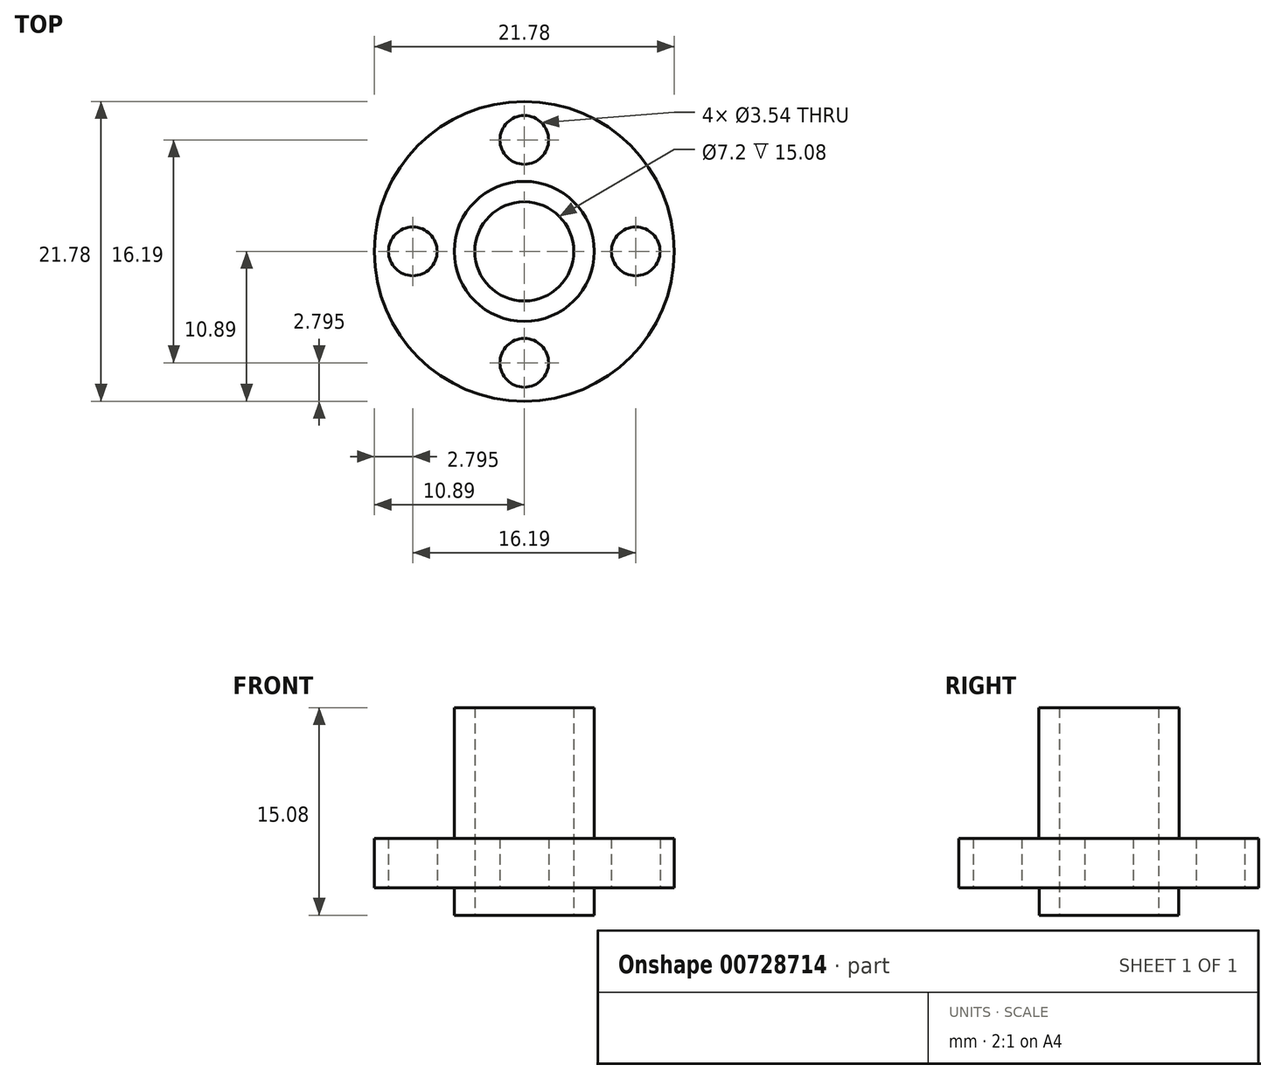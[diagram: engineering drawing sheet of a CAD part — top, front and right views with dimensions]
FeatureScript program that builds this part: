
annotation { "Feature Type Name" : "Feature", "Feature Type Description" : "" }
export const myFeature = defineFeature(function(context is Context, id is Id, definition is map)
    precondition{}
    {
        {
            var Q0;
            Q0=qCreatedBy(makeId("Top.planeOp"),FACE);
            var sketch = newSketch(context, id + "F0", { "sketchPlane" : qUnion([Q0])});
            skCircle(sketch, "E0", {"center": v(0, 0) * mm, "radius": 10.9 * mm});
            skCircle(sketch, "E1", {"center": v(0, 0) * mm, "radius": 8.1 * mm, "construction": true});
            skCircle(sketch, "E2", {"center": v(0, 8.1) * mm, "radius": 1.77 * mm});
            skCircle(sketch, "E3.1.0", {"center": v(8.1, 0) * mm, "radius": 1.77 * mm});
            skCircle(sketch, "E3.2.0", {"center": v(0, -8.1) * mm, "radius": 1.77 * mm});
            skCircle(sketch, "E3.3.0", {"center": v(-8.1, 0) * mm, "radius": 1.77 * mm});
            skLineSegment(sketch, "E3.anchor1", {"start": v(0, 0) * mm, "end": v(0, 8.1) * mm, "construction": true});
            skLineSegment(sketch, "E3.anchor2", {"start": v(0, 0) * mm, "end": v(-8.1, 0) * mm, "construction": true});
            skCircle(sketch, "E4", {"center": v(0, 0) * mm, "radius": 3.6 * mm});
            skSolve(sketch);
        }
        {
            var Q0;
            Q0=makeQuery(id+"F0.imprint","IMPRINT",FACE,{"disambiguationData":[TD([[makeQuery(id+"F0.imprint","IMPRINT",EDGE,{"derivedFrom":sQuery(id+"F0.wireOp",EDGE,"E0")}),1.0]])]});
            extrude(context, id + "F1", {"entities" : qUnion([Q0]), "depth" : 3.58 * mm, "offsetDistance" : 25 * mm});
        }
        {
            var Q0;
            Q0=makeQuery(id+"F1.opExtrude","CAP_FACE",FACE,{"disambiguationData":[OSD([sQuery(id+"F0.wireOp",EDGE,"E0"),sQuery(id+"F0.wireOp",EDGE,"E2"),sQuery(id+"F0.wireOp",EDGE,"E3.1.0"),sQuery(id+"F0.wireOp",EDGE,"E3.2.0"),sQuery(id+"F0.wireOp",EDGE,"E3.3.0"),sQuery(id+"F0.wireOp",EDGE,"E4")])],"isStart":true});
            var sketch = newSketch(context, id + "F2", { "sketchPlane" : qUnion([Q0])});
            skCircle(sketch, "E5", {"center": v(0, 0) * mm, "radius": 5.08 * mm});
            skSolve(sketch);
        }
        {
            var Q0;
            Q0=makeQuery(id+"F2.imprint","IMPRINT",FACE,{"disambiguationData":[TD([[makeQuery(id+"F2.imprint","IMPRINT",EDGE,{"derivedFrom":sQuery(id+"F2.wireOp",EDGE,"E5")}),1.0]])]});
            extrude(context, id + "F3", {"entities" : qUnion([Q0]), "operationType" : NewBodyOperationType.ADD, "depth" : 2 * mm, "offsetDistance" : 25 * mm});
        }
        {
            var Q0;
            Q0=makeQuery(id+"F1.opExtrude","CAP_FACE",FACE,{"disambiguationData":[OSD([sQuery(id+"F0.wireOp",EDGE,"E0"),sQuery(id+"F0.wireOp",EDGE,"E2"),sQuery(id+"F0.wireOp",EDGE,"E3.1.0"),sQuery(id+"F0.wireOp",EDGE,"E3.2.0"),sQuery(id+"F0.wireOp",EDGE,"E3.3.0"),sQuery(id+"F0.wireOp",EDGE,"E4")])],"isStart":false});
            var sketch = newSketch(context, id + "F4", { "sketchPlane" : qUnion([Q0])});
            skCircle(sketch, "E6", {"center": v(0, 0) * mm, "radius": 5.08 * mm});
            skSolve(sketch);
        }
        {
            var Q0;
            Q0=makeQuery(id+"F4.imprint","IMPRINT",FACE,{"disambiguationData":[TD([[makeQuery(id+"F4.imprint","IMPRINT",EDGE,{"derivedFrom":sQuery(id+"F4.wireOp",EDGE,"E6")}),1.0]])]});
            extrude(context, id + "F5", {"entities" : qUnion([Q0]), "operationType" : NewBodyOperationType.ADD, "depth" : 9.5 * mm, "offsetDistance" : 25 * mm});
        }
    });
